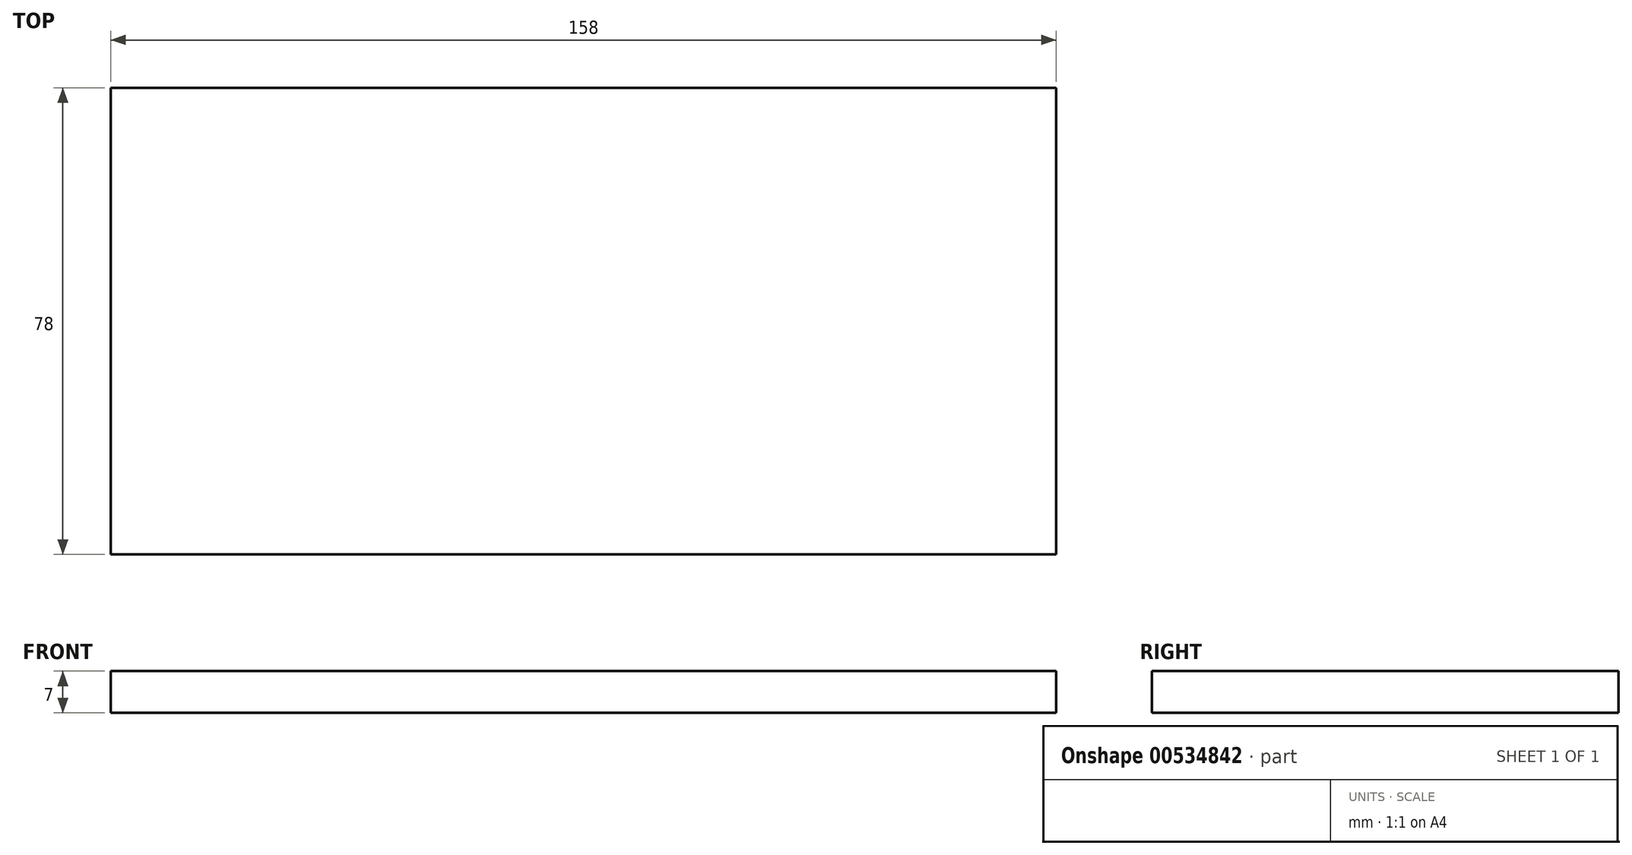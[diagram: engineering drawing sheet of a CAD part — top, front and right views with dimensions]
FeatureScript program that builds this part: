
annotation { "Feature Type Name" : "Feature", "Feature Type Description" : "" }
export const myFeature = defineFeature(function(context is Context, id is Id, definition is map)
    precondition{}
    {
        {
            var Q0;
            Q0=qCreatedBy(makeId("Top.planeOp"),FACE);
            var sketch = newSketch(context, id + "F0", { "sketchPlane" : qUnion([Q0])});
            skLineSegment(sketch, "E0.bottom", {"start": v(79, -39) * mm, "end": v(-79, -39) * mm});
            skLineSegment(sketch, "E0.top", {"start": v(79, 39) * mm, "end": v(-79, 39) * mm});
            skLineSegment(sketch, "E0.left", {"start": v(79, -39) * mm, "end": v(79, 39) * mm});
            skLineSegment(sketch, "E0.right", {"start": v(-79, -39) * mm, "end": v(-79, 39) * mm});
            skPoint(sketch, "E0.middle", {"position": v(0, 0) * mm});
            skSolve(sketch);
        }
        {
            var Q0;
            Q0=makeQuery(id+"F0.imprint","IMPRINT",FACE,{"disambiguationData":[TD([[makeQuery(id+"F0.imprint","IMPRINT",EDGE,{"derivedFrom":sQuery(id+"F0.wireOp",EDGE,"E0.bottom")}),-1.0]])]});
            extrude(context, id + "F1", {"entities" : qUnion([Q0]), "depth" : 7 * mm, "offsetDistance" : 25 * mm});
        }
    });
